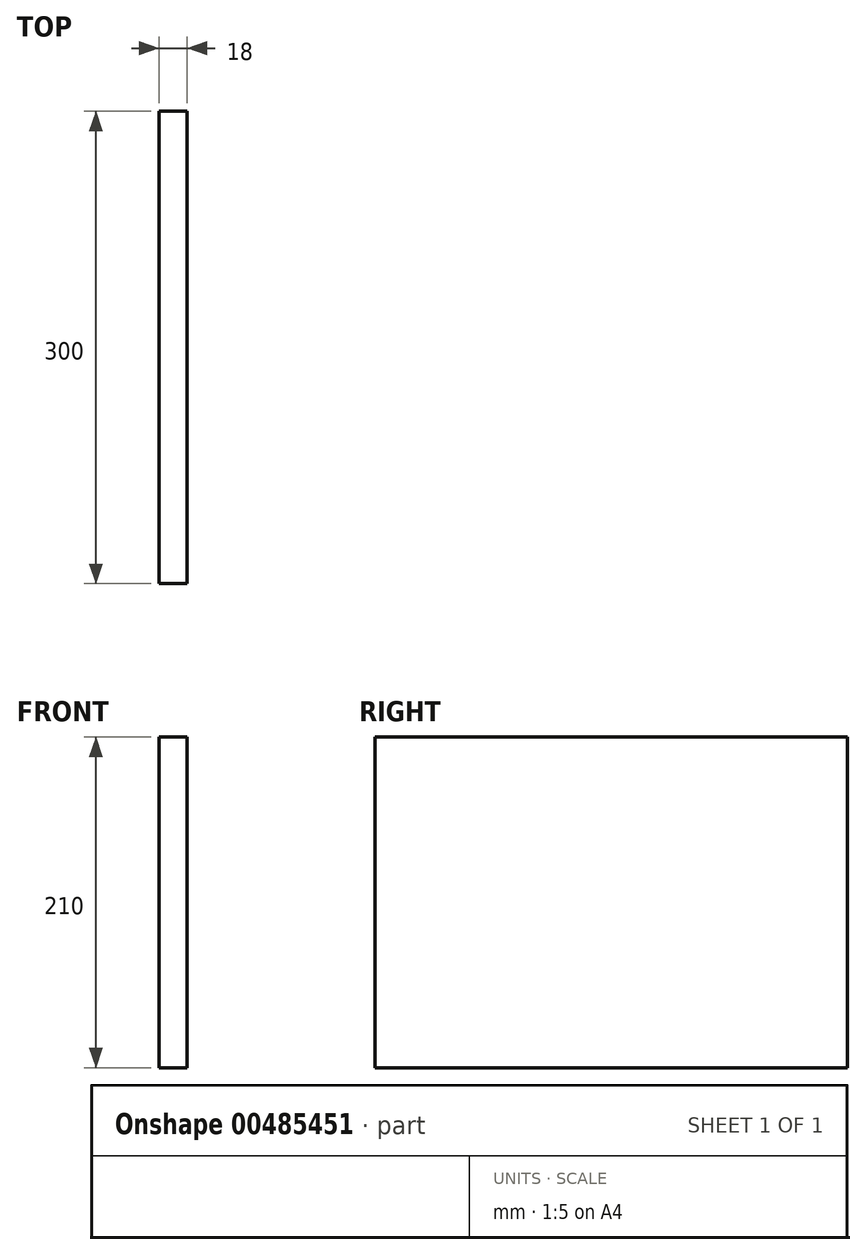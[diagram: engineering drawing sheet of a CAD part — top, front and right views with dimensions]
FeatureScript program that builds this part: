
annotation { "Feature Type Name" : "Feature", "Feature Type Description" : "" }
export const myFeature = defineFeature(function(context is Context, id is Id, definition is map)
    precondition{}
    {
        {
            var Q0;
            Q0=qCreatedBy(makeId("Top.planeOp"),FACE);
            var sketch = newSketch(context, id + "F0", { "sketchPlane" : qUnion([Q0])});
            skLineSegment(sketch, "E0.bottom", {"start": v(9, 150) * mm, "end": v(-9, 150) * mm});
            skLineSegment(sketch, "E0.top", {"start": v(9, -150) * mm, "end": v(-9, -150) * mm});
            skLineSegment(sketch, "E0.left", {"start": v(9, 150) * mm, "end": v(9, -150) * mm});
            skLineSegment(sketch, "E0.right", {"start": v(-9, 150) * mm, "end": v(-9, -150) * mm});
            skPoint(sketch, "E0.middle", {"position": v(0, 0) * mm});
            skSolve(sketch);
        }
        {
            var Q0;
            Q0 = qSketchRegion(id + "F0", true);
            extrude(context, id + "F1", {"entities" : qUnion([Q0]), "depth" : 210 * mm});
        }
    });
